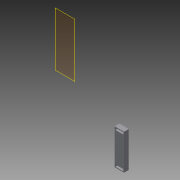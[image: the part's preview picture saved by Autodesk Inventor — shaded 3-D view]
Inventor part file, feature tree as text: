
AUTODESK INVENTOR PART (.ipt)
format: ipt  version: 2015 (Build 190159000, 159)  size: 87,552 bytes
history: native  units: in
note: dims shown in document units (in); Inventor stores cm internally (conversion verified against a paired STEP export)
features: extrude x2, sketch x2, reference x2, plane x1
ambient origin geometry x8: Origin, YZ Plane, XZ Plane, XY Plane, X Axis, Y Axis, Z Axis, Center Point
bodies: Solid1 (feature_tree)
feature tree (7):
  plane  "Work Plane1"
  extrude  "Extrusion1"  Depth=0.1in TaperAngle=0.0deg
  extrude  "Extrusion2"  [1 undecoded]
  sketch  "Sketch1"  dims[d2=0.5in d3=0.0in d4=0.1in d5=0.0in]
  reference  "Reference1"
  reference  "Reference2"
  sketch  "Sketch2"
note: 1 required parameter value undecoded (feature->parameter linkage not recoverable at this tier; creation-order binding heuristic only, values carry confidence <= 0.55)
